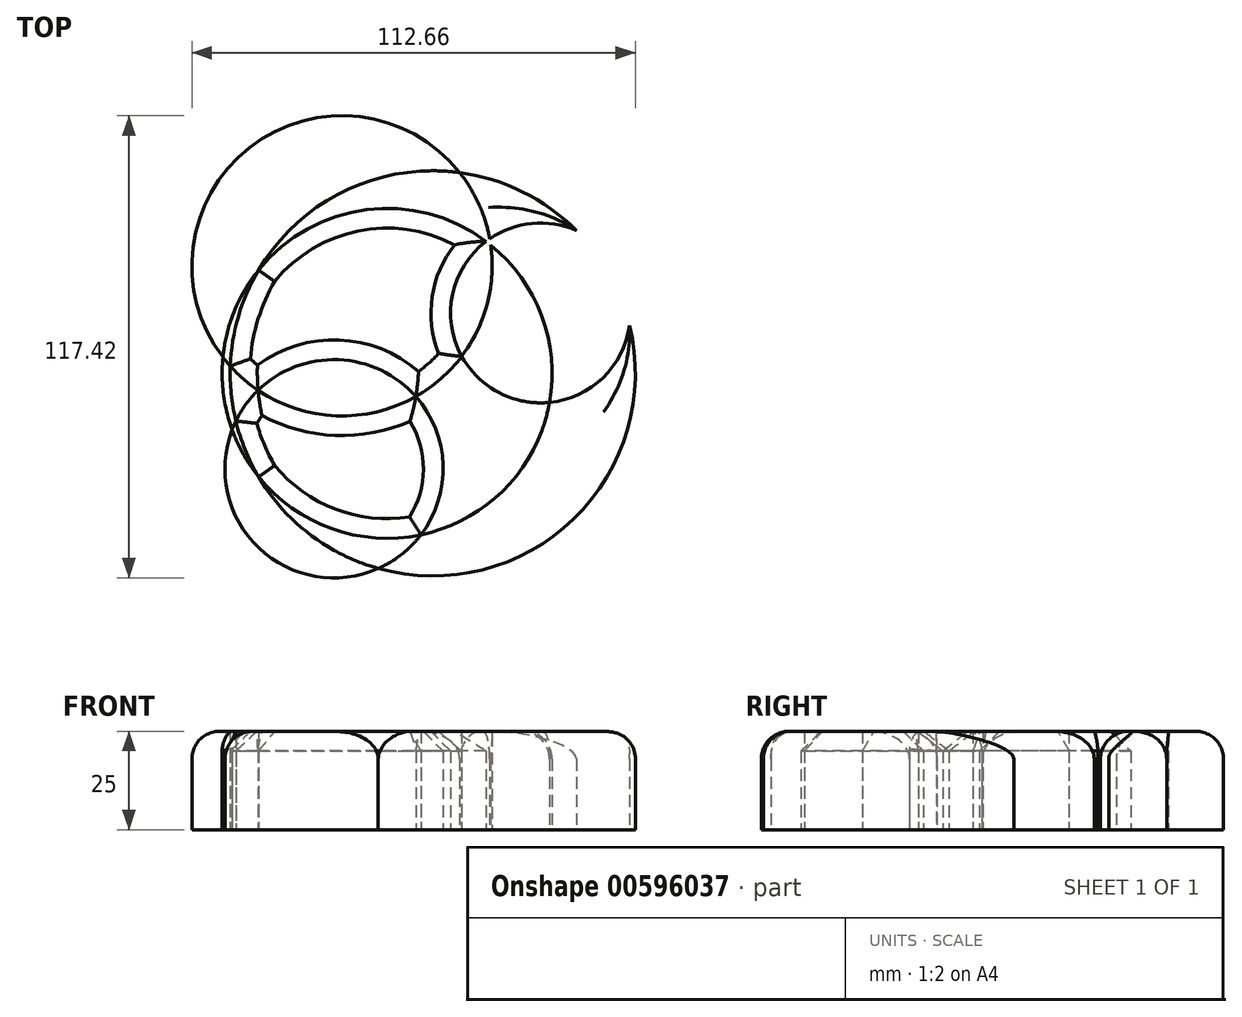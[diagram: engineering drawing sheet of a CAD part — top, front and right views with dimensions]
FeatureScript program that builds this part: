
annotation { "Feature Type Name" : "Feature", "Feature Type Description" : "" }
export const myFeature = defineFeature(function(context is Context, id is Id, definition is map)
    precondition{}
    {
        {
            var Q0;
            Q0=qCreatedBy(makeId("Top.planeOp"),FACE);
            var sketch = newSketch(context, id + "F0", { "sketchPlane" : qUnion([Q0])});
            skCircle(sketch, "E0", {"center": v(0, 0) * mm, "radius": 51.47 * mm});
            skCircle(sketch, "E1", {"center": v(27.38, 15.35) * mm, "radius": 22.85 * mm});
            skCircle(sketch, "E2", {"center": v(-25.1, -24.23) * mm, "radius": 27.73 * mm});
            skCircle(sketch, "E3", {"center": v(-23.06, 27.32) * mm, "radius": 38.13 * mm});
            skCircle(sketch, "E4", {"center": v(-11.6, 0) * mm, "radius": 41.9 * mm});
            skSolve(sketch);
        }
        {
            var Q0;
            {var subQ0=sQuery(id+"F0.wireOp",EDGE,"E1");var subQ1=sQuery(id+"F0.wireOp",EDGE,"E0");var subQ2=makeQuery(id+"F0.imprint","INTERSECT",VERTEX,{"disambiguationData":[OD(1.0)],"derivedFrom":[subQ1,subQ0]});Q0=makeQuery(id+"F0.imprint","IMPRINT",FACE,{"disambiguationData":[TD([[makeQuery(id+"F0.imprint","IMPRINT",EDGE,{"disambiguationData":[TD([[subQ2,1.0]])],"derivedFrom":subQ1}),1.0]])]});}
            var Q1;
            {var subQ1=sQuery(id+"F0.wireOp",EDGE,"E2");var subQ6=sQuery(id+"F0.wireOp",EDGE,"E0");var subQ7=makeQuery(id+"F0.imprint","INTERSECT",VERTEX,{"disambiguationData":[OD(1.0)],"derivedFrom":[subQ6,subQ1]});Q1=makeQuery(id+"F0.imprint","IMPRINT",FACE,{"disambiguationData":[TD([[makeQuery(id+"F0.imprint","IMPRINT",EDGE,{"disambiguationData":[TD([[subQ7,-1.0]])],"derivedFrom":subQ6}),1.0]])]});}
            var Q2;
            {var subQ0=sQuery(id+"F0.wireOp",EDGE,"E2");var subQ1=sQuery(id+"F0.wireOp",EDGE,"E0");var subQ2=makeQuery(id+"F0.imprint","INTERSECT",VERTEX,{"disambiguationData":[OD(0.0)],"derivedFrom":[subQ1,subQ0]});Q2=makeQuery(id+"F0.imprint","IMPRINT",FACE,{"disambiguationData":[TD([[makeQuery(id+"F0.imprint","IMPRINT",EDGE,{"disambiguationData":[TD([[subQ2,1.0]])],"derivedFrom":subQ1}),-1.0]])]});}
            var Q3;
            {var subQ0=sQuery(id+"F0.wireOp",EDGE,"E3");var subQ1=sQuery(id+"F0.wireOp",EDGE,"E1");var subQ2=makeQuery(id+"F0.imprint","INTERSECT",VERTEX,{"disambiguationData":[OD(1.0)],"derivedFrom":[subQ1,subQ0]});Q3=makeQuery(id+"F0.imprint","IMPRINT",FACE,{"disambiguationData":[TD([[makeQuery(id+"F0.imprint","IMPRINT",EDGE,{"disambiguationData":[TD([[subQ2,-1.0]])],"derivedFrom":subQ1}),1.0]])]});}
            var Q4;
            {var subQ1=sQuery(id+"F0.wireOp",EDGE,"E0");var subQ6=sQuery(id+"F0.wireOp",EDGE,"E4");var subQ7=makeQuery(id+"F0.imprint","INTERSECT",VERTEX,{"disambiguationData":[OD(0.0)],"derivedFrom":[subQ1,subQ6]});Q4=makeQuery(id+"F0.imprint","IMPRINT",FACE,{"disambiguationData":[TD([[makeQuery(id+"F0.imprint","IMPRINT",EDGE,{"disambiguationData":[TD([[subQ7,-1.0]])],"derivedFrom":subQ1}),1.0]])]});}
            var Q5;
            {var subQ0=sQuery(id+"F0.wireOp",EDGE,"E3");var subQ1=sQuery(id+"F0.wireOp",EDGE,"E0");var subQ2=makeQuery(id+"F0.imprint","INTERSECT",VERTEX,{"disambiguationData":[OD(0.0)],"derivedFrom":[subQ1,subQ0]});Q5=makeQuery(id+"F0.imprint","IMPRINT",FACE,{"disambiguationData":[TD([[makeQuery(id+"F0.imprint","IMPRINT",EDGE,{"disambiguationData":[TD([[subQ2,-1.0]])],"derivedFrom":subQ1}),-1.0]])]});}
            var Q6;
            {var subQ0=sQuery(id+"F0.wireOp",EDGE,"E3");var subQ1=sQuery(id+"F0.wireOp",EDGE,"E0");var subQ2=makeQuery(id+"F0.imprint","INTERSECT",VERTEX,{"disambiguationData":[OD(1.0)],"derivedFrom":[subQ1,subQ0]});Q6=makeQuery(id+"F0.imprint","IMPRINT",FACE,{"disambiguationData":[TD([[makeQuery(id+"F0.imprint","IMPRINT",EDGE,{"disambiguationData":[TD([[subQ2,-1.0]])],"derivedFrom":subQ1}),-1.0]])]});}
            var Q7;
            {var subQ0=sQuery(id+"F0.wireOp",EDGE,"E1");var subQ1=sQuery(id+"F0.wireOp",EDGE,"E0");var subQ2=makeQuery(id+"F0.imprint","INTERSECT",VERTEX,{"disambiguationData":[OD(0.0)],"derivedFrom":[subQ1,subQ0]});Q7=makeQuery(id+"F0.imprint","IMPRINT",FACE,{"disambiguationData":[TD([[makeQuery(id+"F0.imprint","IMPRINT",EDGE,{"disambiguationData":[TD([[subQ2,-1.0]])],"derivedFrom":subQ1}),1.0]])]});}
            extrude(context, id + "F1", {"entities" : qUnion([Q0, Q1, Q2, Q3, Q4, Q5, Q6, Q7]), "depth" : 25 * mm, "offsetDistance" : 25 * mm});
        }
        {
            var Q0;
            {var subQ0=sQuery(id+"F0.wireOp",EDGE,"E2");Q0=makeQuery(id+"F1.opExtrude","CAP_EDGE",EDGE,{"disambiguationData":[OSD([subQ0]),TDD([makeQuery(id+"F0.imprint","IMPRINT",EDGE,{"disambiguationData":[TD([[makeQuery(id+"F0.imprint","INTERSECT",VERTEX,{"disambiguationData":[OD(0.0)],"derivedFrom":[sQuery(id+"F0.wireOp",EDGE,"E0"),subQ0]}),1.0]])],"derivedFrom":subQ0})])],"isStart":false});}
            var Q1;
            {var subQ0=sQuery(id+"F0.wireOp",EDGE,"E4");Q1=makeQuery(id+"F1.opExtrude","CAP_EDGE",EDGE,{"disambiguationData":[OSD([subQ0]),TDD([makeQuery(id+"F0.imprint","IMPRINT",EDGE,{"disambiguationData":[TD([[makeQuery(id+"F0.imprint","INTERSECT",VERTEX,{"disambiguationData":[OD(0.0)],"derivedFrom":[sQuery(id+"F0.wireOp",EDGE,"E2"),subQ0]}),1.0]])],"derivedFrom":subQ0})])],"isStart":false});}
            var Q2;
            {var subQ0=sQuery(id+"F0.wireOp",EDGE,"E3");Q2=makeQuery(id+"F1.opExtrude","CAP_EDGE",EDGE,{"disambiguationData":[OSD([subQ0]),TDD([makeQuery(id+"F0.imprint","IMPRINT",EDGE,{"disambiguationData":[TD([[makeQuery(id+"F0.imprint","INTERSECT",VERTEX,{"disambiguationData":[OD(0.0)],"derivedFrom":[sQuery(id+"F0.wireOp",EDGE,"E0"),subQ0]}),-1.0]])],"derivedFrom":subQ0})])],"isStart":false});}
            var Q3;
            {var subQ0=sQuery(id+"F0.wireOp",EDGE,"E0");Q3=makeQuery(id+"F1.opExtrude","CAP_EDGE",EDGE,{"disambiguationData":[OSD([subQ0]),TDD([makeQuery(id+"F0.imprint","IMPRINT",EDGE,{"disambiguationData":[TD([[makeQuery(id+"F0.imprint","INTERSECT",VERTEX,{"disambiguationData":[OD(1.0)],"derivedFrom":[subQ0,sQuery(id+"F0.wireOp",EDGE,"E1")]}),1.0]])],"derivedFrom":subQ0})])],"isStart":false});}
            var Q4;
            {var subQ0=sQuery(id+"F0.wireOp",EDGE,"E0");Q4=makeQuery(id+"F1.opExtrude","CAP_EDGE",EDGE,{"disambiguationData":[OSD([subQ0]),TDD([makeQuery(id+"F0.imprint","IMPRINT",EDGE,{"disambiguationData":[TD([[makeQuery(id+"F0.imprint","INTERSECT",VERTEX,{"disambiguationData":[OD(0.0)],"derivedFrom":[subQ0,sQuery(id+"F0.wireOp",EDGE,"E1")]}),-1.0]])],"derivedFrom":subQ0})])],"isStart":false});}
            var Q5;
            {var subQ0=sQuery(id+"F0.wireOp",EDGE,"E1");Q5=makeQuery(id+"F1.opExtrude","CAP_EDGE",EDGE,{"disambiguationData":[OSD([subQ0]),TDD([makeQuery(id+"F0.imprint","IMPRINT",EDGE,{"disambiguationData":[TD([[makeQuery(id+"F0.imprint","INTERSECT",VERTEX,{"disambiguationData":[OD(0.0)],"derivedFrom":[sQuery(id+"F0.wireOp",EDGE,"E0"),subQ0]}),-1.0]])],"derivedFrom":subQ0})])],"isStart":false});}
            var Q6;
            {var subQ0=sQuery(id+"F0.wireOp",EDGE,"E1");Q6=makeQuery(id+"F1.opExtrude","CAP_EDGE",EDGE,{"disambiguationData":[OSD([subQ0]),TDD([makeQuery(id+"F0.imprint","IMPRINT",EDGE,{"disambiguationData":[TD([[makeQuery(id+"F0.imprint","INTERSECT",VERTEX,{"disambiguationData":[OD(1.0)],"derivedFrom":[sQuery(id+"F0.wireOp",EDGE,"E0"),subQ0]}),1.0]])],"derivedFrom":subQ0})])],"isStart":false});}
            var Q7;
            {var subQ0=sQuery(id+"F0.wireOp",EDGE,"E4");Q7=makeQuery(id+"F1.opExtrude","CAP_EDGE",EDGE,{"disambiguationData":[OSD([subQ0]),TDD([makeQuery(id+"F0.imprint","IMPRINT",EDGE,{"disambiguationData":[TD([[makeQuery(id+"F0.imprint","INTERSECT",VERTEX,{"disambiguationData":[OD(1.0)],"derivedFrom":[sQuery(id+"F0.wireOp",EDGE,"E1"),subQ0]}),-1.0]])],"derivedFrom":subQ0})])],"isStart":false});}
            fillet(context, id + "F2", {"entities" : qUnion([Q0, Q1, Q2, Q3, Q4, Q5, Q6, Q7]), "radius" : 7 * mm, "tangentPropagation" : true, "allowEdgeOverflow" : false});
        }
        {
            var Q0;
            {var subQ0=sQuery(id+"F0.wireOp",EDGE,"E4");Q0=makeQuery(id+"F1.opExtrude","CAP_EDGE",EDGE,{"disambiguationData":[OSD([subQ0]),TDD([makeQuery(id+"F0.imprint","IMPRINT",EDGE,{"disambiguationData":[TD([[makeQuery(id+"F0.imprint","INTERSECT",VERTEX,{"disambiguationData":[OD(0.0)],"derivedFrom":[sQuery(id+"F0.wireOp",EDGE,"E0"),subQ0]}),1.0]])],"derivedFrom":subQ0})])],"isStart":false});}
            var Q1;
            {var subQ0=sQuery(id+"F0.wireOp",EDGE,"E3");var subQ1=sQuery(id+"F0.wireOp",EDGE,"E2");Q1=makeQuery(id+"F1.opExtrude","CAP_EDGE",EDGE,{"disambiguationData":[OSD([subQ0]),TDD([makeQuery(id+"F0.imprint","IMPRINT",EDGE,{"disambiguationData":[TD([[makeQuery(id+"F0.imprint","INTERSECT",VERTEX,{"disambiguationData":[OD(0.0)],"derivedFrom":[subQ1,subQ0]}),-1.0]])],"derivedFrom":subQ0})])],"isStart":false});}
            var Q2;
            {var subQ0=sQuery(id+"F0.wireOp",EDGE,"E2");Q2=makeQuery(id+"F1.opExtrude","CAP_EDGE",EDGE,{"disambiguationData":[OSD([subQ0]),TDD([makeQuery(id+"F0.imprint","IMPRINT",EDGE,{"disambiguationData":[TD([[makeQuery(id+"F0.imprint","INTERSECT",VERTEX,{"disambiguationData":[OD(1.0)],"derivedFrom":[subQ0,sQuery(id+"F0.wireOp",EDGE,"E3")]}),1.0]])],"derivedFrom":subQ0})])],"isStart":false});}
            var Q3;
            {var subQ0=sQuery(id+"F0.wireOp",EDGE,"E1");Q3=makeQuery(id+"F1.opExtrude","CAP_EDGE",EDGE,{"disambiguationData":[OSD([subQ0]),TDD([makeQuery(id+"F0.imprint","IMPRINT",EDGE,{"disambiguationData":[TD([[makeQuery(id+"F0.imprint","INTERSECT",VERTEX,{"disambiguationData":[OD(0.0)],"derivedFrom":[subQ0,sQuery(id+"F0.wireOp",EDGE,"E4")]}),-1.0]])],"derivedFrom":subQ0})])],"isStart":false});}
            var Q4;
            {var subQ0=sQuery(id+"F0.wireOp",EDGE,"E2");Q4=makeQuery(id+"F1.opExtrude","CAP_EDGE",EDGE,{"disambiguationData":[OSD([subQ0]),TDD([makeQuery(id+"F0.imprint","IMPRINT",EDGE,{"disambiguationData":[TD([[makeQuery(id+"F0.imprint","INTERSECT",VERTEX,{"disambiguationData":[OD(1.0)],"derivedFrom":[sQuery(id+"F0.wireOp",EDGE,"E0"),subQ0]}),1.0]])],"derivedFrom":subQ0})])],"isStart":false});}
            var Q5;
            {var subQ0=sQuery(id+"F0.wireOp",EDGE,"E3");var subQ1=sQuery(id+"F0.wireOp",EDGE,"E2");Q5=makeQuery(id+"F1.opExtrude","CAP_EDGE",EDGE,{"disambiguationData":[OSD([subQ1]),TDD([makeQuery(id+"F0.imprint","IMPRINT",EDGE,{"disambiguationData":[TD([[makeQuery(id+"F0.imprint","INTERSECT",VERTEX,{"disambiguationData":[OD(0.0)],"derivedFrom":[subQ1,subQ0]}),1.0]])],"derivedFrom":subQ1})])],"isStart":false});}
            var Q6;
            {var subQ0=sQuery(id+"F0.wireOp",EDGE,"E3");Q6=makeQuery(id+"F1.opExtrude","CAP_EDGE",EDGE,{"disambiguationData":[OSD([subQ0]),TDD([makeQuery(id+"F0.imprint","IMPRINT",EDGE,{"disambiguationData":[TD([[makeQuery(id+"F0.imprint","INTERSECT",VERTEX,{"disambiguationData":[OD(1.0)],"derivedFrom":[sQuery(id+"F0.wireOp",EDGE,"E0"),subQ0]}),-1.0]])],"derivedFrom":subQ0})])],"isStart":false});}
            var Q7;
            {var subQ0=sQuery(id+"F0.wireOp",EDGE,"E3");Q7=makeQuery(id+"F1.opExtrude","CAP_EDGE",EDGE,{"disambiguationData":[OSD([subQ0]),TDD([makeQuery(id+"F0.imprint","IMPRINT",EDGE,{"disambiguationData":[TD([[makeQuery(id+"F0.imprint","INTERSECT",VERTEX,{"disambiguationData":[OD(1.0)],"derivedFrom":[sQuery(id+"F0.wireOp",EDGE,"E1"),subQ0]}),1.0]])],"derivedFrom":subQ0})])],"isStart":false});}
            var Q8;
            {var subQ0=sQuery(id+"F0.wireOp",EDGE,"E0");Q8=makeQuery(id+"F1.opExtrude","CAP_EDGE",EDGE,{"disambiguationData":[OSD([subQ0]),TDD([makeQuery(id+"F0.imprint","IMPRINT",EDGE,{"disambiguationData":[TD([[makeQuery(id+"F0.imprint","INTERSECT",VERTEX,{"disambiguationData":[OD(0.0)],"derivedFrom":[subQ0,sQuery(id+"F0.wireOp",EDGE,"E4")]}),-1.0]])],"derivedFrom":subQ0})])],"isStart":false});}
            var Q9;
            {var subQ0=sQuery(id+"F0.wireOp",EDGE,"E4");Q9=makeQuery(id+"F1.opExtrude","CAP_EDGE",EDGE,{"disambiguationData":[OSD([subQ0]),TDD([makeQuery(id+"F0.imprint","IMPRINT",EDGE,{"disambiguationData":[TD([[makeQuery(id+"F0.imprint","INTERSECT",VERTEX,{"disambiguationData":[OD(1.0)],"derivedFrom":[sQuery(id+"F0.wireOp",EDGE,"E0"),subQ0]}),-1.0]])],"derivedFrom":subQ0})])],"isStart":false});}
            var Q10;
            {var subQ0=sQuery(id+"F0.wireOp",EDGE,"E0");Q10=makeQuery(id+"F1.opExtrude","CAP_EDGE",EDGE,{"disambiguationData":[OSD([subQ0]),TDD([makeQuery(id+"F0.imprint","IMPRINT",EDGE,{"disambiguationData":[TD([[makeQuery(id+"F0.imprint","INTERSECT",VERTEX,{"disambiguationData":[OD(1.0)],"derivedFrom":[subQ0,sQuery(id+"F0.wireOp",EDGE,"E2")]}),-1.0]])],"derivedFrom":subQ0})])],"isStart":false});}
            chamfer(context, id + "F3", {"entities" : qUnion([Q0, Q1, Q2, Q3, Q4, Q5, Q6, Q7, Q8, Q9, Q10]), "width" : 5 * mm, "tangentPropagation" : true});
        }
    });
